# Revit family: window_dbl-hung 1-unit v2013dan
name_source: partatom
category: Windows
revit_build: Autodesk Revit Architecture 2013 (Build: 20130531_2115(x64)
units: mm (PartAtom-declared; Revit-internal decimal feet)

## types (1)
- exist 2-6 x 4-0
    Analytic Construction = <None>
    Assembly Code = B2020100
    Description = x
    Height = 4' - 1 1/2"
    Keynote = 08500.WD
    Manufacturer = x
    Model = x
    Wall Closure = By host
    Width = 2' - 7 1/2"
    default sash height yN = Yes
    ext cap trim yN = No
    ext face offset = 4"
    frame exterior = <By Category>
    frame interior = <By Category>
    glass = Glass
    grill width = 3/4"
    grille lower yN = Yes
    grille spaces_horiz = 3
    grille spaces_vert lower = 2
    grille spaces_vert upper = 2
    grille upper yN = Yes
    shutter color = 08550 window shutter solid- existing
    shutter face offset = 2"
    shutter side offset = 0"
    shutterW = 1' - 5"
    trim depth- exterior = 2"
    trim exterior = <By Category>
    trim interior = <By Category>
    trim width- exterior = 5"
    trim width- interior = 4"
    upper sash height = 2' - 0"

## geometry (parser evidence)
native form markers: Blend x8, Sweep x8
no freeform markers — native parametric forms only
